# Revit family: ML_IMC3_LUX
name_source: partatom
category: Specialty Equipment
units: mm (PartAtom-declared; Revit-internal decimal feet)

## family parameters
Always vertical = Yes
Cut with Voids When Loaded = No
OmniClass Number = 23.40.20.21.47
OmniClass Title = Bath Grab Bars
Part Type = Normal
Room Calculation Point = No
Round Connector Dimension = Use Diameter
Shared = No
Work Plane-Based = No

## types (1)
- ML_IMC3_LUX
    Assembly Code = C1030200
    Bolts = z_Metlam_Stainless Steel
    Description = 30° Flush Mount Side Wall & Cistern Grab Rail LH Set
    Frame = Aluminium
    Jar = Plastic
    Manufacture Depth = 125 mm
    Manufacture Height = 859 mm  [stored 2.81824 ft]
    Manufacture Width = 865 mm
    Manufacturer = Metlam
    Manufacturer_Spec Code = MLR 101
    Manufacturer_URL_Home Page = http://www.metlam.com.au
    Manufacturer_URL__Product Specific = http://metlam.com.au
    Mirror = Mirror
    Model = MLR 101
    ModifiedIssue_ANZRS = 20151029 $
    Type Comments = Grab Rails
    URL = http://www.metlam.com.au

note: [stored X ft] marks values corroborated as IEEE doubles in the binary element streams (Revit-internal decimal feet)

## geometry (parser evidence)
native form markers: Sweep x7
no freeform markers — native parametric forms only
